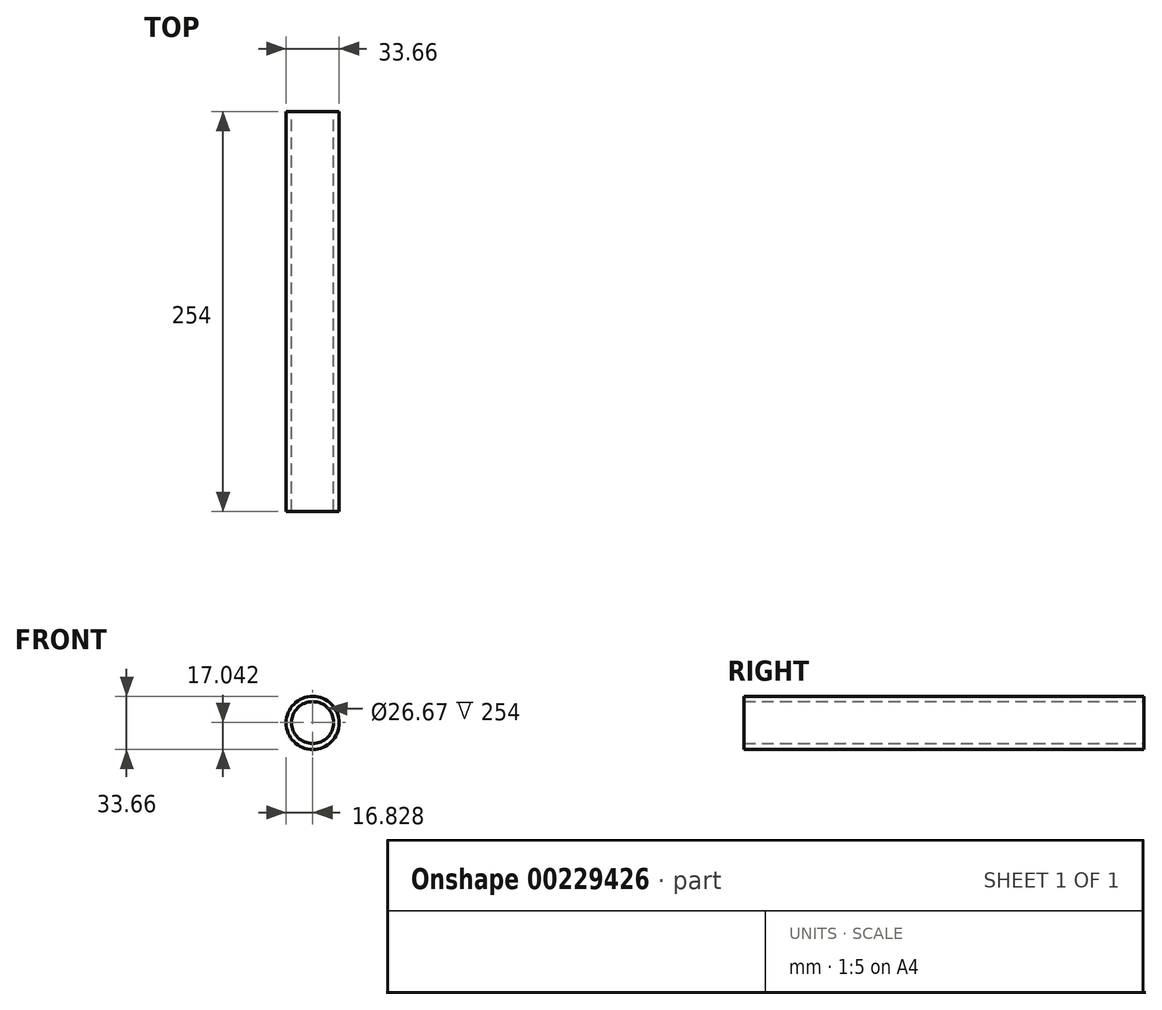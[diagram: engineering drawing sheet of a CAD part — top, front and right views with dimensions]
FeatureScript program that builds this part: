
annotation { "Feature Type Name" : "Feature", "Feature Type Description" : "" }
export const myFeature = defineFeature(function(context is Context, id is Id, definition is map)
    precondition{}
    {
        {
            var Q0;
            Q0=qCreatedBy(makeId("Front.planeOp"),FACE);
            var sketch = newSketch(context, id + "F0", { "sketchPlane" : qUnion([Q0])});
            skCircle(sketch, "E0", {"center": v(-0.18, 0.12) * mm, "radius": 13.34 * mm});
            skCircle(sketch, "E1", {"center": v(-0.18, -0.1) * mm, "radius": 16.83 * mm});
            skSolve(sketch);
        }
        {
            var Q0;
            Q0=makeQuery(id+"F0.imprint","IMPRINT",FACE,{"disambiguationData":[TD([[makeQuery(id+"F0.imprint","IMPRINT",EDGE,{"derivedFrom":sQuery(id+"F0.wireOp",EDGE,"E0")}),-1.0]])]});
            extrude(context, id + "F1", {"entities" : qUnion([Q0]), "depth" : 254 * mm});
        }
    });
